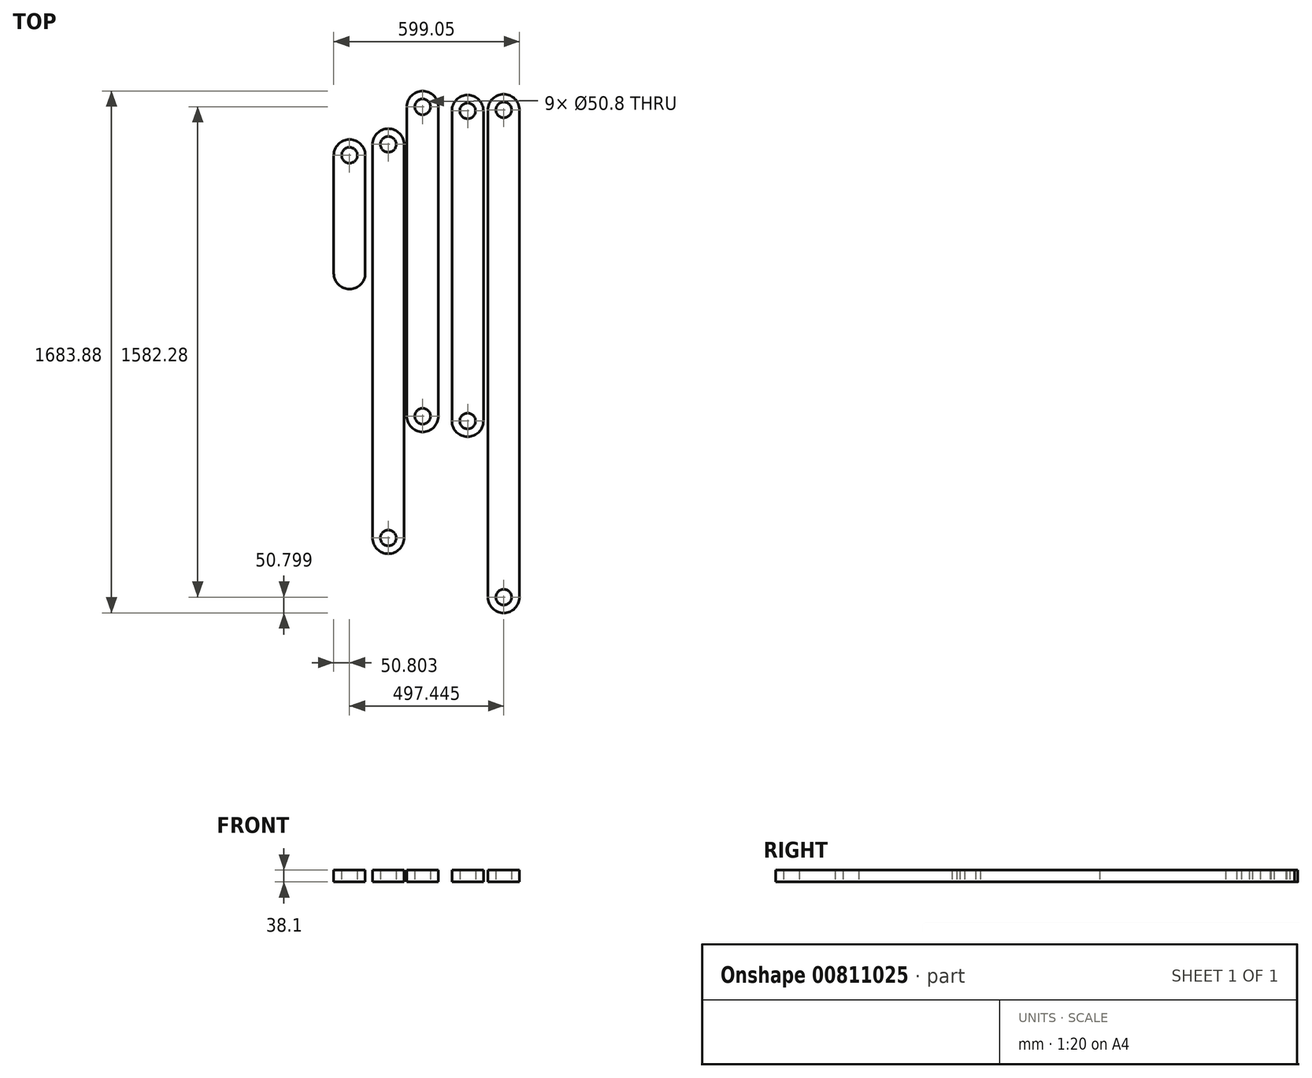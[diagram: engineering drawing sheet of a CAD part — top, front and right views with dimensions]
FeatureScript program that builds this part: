
annotation { "Feature Type Name" : "Feature", "Feature Type Description" : "" }
export const myFeature = defineFeature(function(context is Context, id is Id, definition is map)
    precondition{}
    {
        {
            var Q0;
            Q0=qCreatedBy(makeId("Top.planeOp"),FACE);
            var sketch = newSketch(context, id + "F0", { "sketchPlane" : qUnion([Q0])});
            skLineSegment(sketch, "E0", {"start": v(237.66, -949.52) * mm, "end": v(237.66, 51.24) * mm});
            skLineSegment(sketch, "E1", {"start": v(339.26, -949.52) * mm, "end": v(339.26, 51.24) * mm});
            skArc(sketch, "E2", {"start": v(237.66, -949.52) * mm, "mid": v(288.46, -1000.32) * mm, "end": v(339.26, -949.52) * mm});
            skArc(sketch, "E3", {"start": v(339.26, 51.24) * mm, "mid": v(288.46, 102.04) * mm, "end": v(237.66, 51.24) * mm});
            skLineSegment(sketch, "E4", {"start": v(237.66, 51.24) * mm, "end": v(339.26, 51.24) * mm, "construction": true});
            skLineSegment(sketch, "E5", {"start": v(237.66, -949.52) * mm, "end": v(339.26, -949.52) * mm, "construction": true});
            skLineSegment(sketch, "E6", {"start": v(-143.46, -473.04) * mm, "end": v(-143.46, -92.04) * mm});
            skLineSegment(sketch, "E7", {"start": v(-41.86, -473.04) * mm, "end": v(-41.86, -92.04) * mm});
            skArc(sketch, "E8", {"start": v(-143.46, -473.04) * mm, "mid": v(-92.66, -523.84) * mm, "end": v(-41.86, -473.04) * mm});
            skArc(sketch, "E9", {"start": v(-41.86, -92.04) * mm, "mid": v(-92.66, -41.24) * mm, "end": v(-143.46, -92.04) * mm});
            skLineSegment(sketch, "E10", {"start": v(-143.46, -92.04) * mm, "end": v(-41.86, -92.04) * mm, "construction": true});
            skLineSegment(sketch, "E11", {"start": v(-143.46, -473.04) * mm, "end": v(-41.86, -473.04) * mm, "construction": true});
            skLineSegment(sketch, "E12", {"start": v(92.52, -933.87) * mm, "end": v(92.52, 64.35) * mm});
            skLineSegment(sketch, "E13", {"start": v(194.12, -933.87) * mm, "end": v(194.12, 64.35) * mm});
            skArc(sketch, "E14", {"start": v(92.52, -933.87) * mm, "mid": v(143.32, -984.67) * mm, "end": v(194.12, -933.87) * mm});
            skArc(sketch, "E15", {"start": v(194.12, 64.35) * mm, "mid": v(143.32, 115.15) * mm, "end": v(92.52, 64.35) * mm});
            skLineSegment(sketch, "E16", {"start": v(92.52, 64.35) * mm, "end": v(194.12, 64.35) * mm, "construction": true});
            skLineSegment(sketch, "E17", {"start": v(92.52, -933.87) * mm, "end": v(194.12, -933.87) * mm, "construction": true});
            skLineSegment(sketch, "E18", {"start": v(-18.26, -1326.87) * mm, "end": v(-18.26, -56.87) * mm});
            skLineSegment(sketch, "E19", {"start": v(83.34, -1326.87) * mm, "end": v(83.34, -56.87) * mm});
            skArc(sketch, "E20", {"start": v(-18.26, -1326.87) * mm, "mid": v(32.54, -1377.67) * mm, "end": v(83.34, -1326.87) * mm});
            skArc(sketch, "E21", {"start": v(83.34, -56.87) * mm, "mid": v(32.54, -6.07) * mm, "end": v(-18.26, -56.87) * mm});
            skLineSegment(sketch, "E22", {"start": v(-18.26, -56.87) * mm, "end": v(83.34, -56.87) * mm, "construction": true});
            skLineSegment(sketch, "E23", {"start": v(-18.26, -1326.87) * mm, "end": v(83.34, -1326.87) * mm, "construction": true});
            skLineSegment(sketch, "E24", {"start": v(353.99, -1517.93) * mm, "end": v(353.99, 54.33) * mm});
            skLineSegment(sketch, "E25", {"start": v(455.59, -1517.93) * mm, "end": v(455.59, 54.33) * mm});
            skArc(sketch, "E26", {"start": v(353.99, -1517.93) * mm, "mid": v(404.79, -1568.73) * mm, "end": v(455.59, -1517.93) * mm});
            skArc(sketch, "E27", {"start": v(455.59, 54.33) * mm, "mid": v(404.79, 105.13) * mm, "end": v(353.99, 54.33) * mm});
            skLineSegment(sketch, "E28", {"start": v(353.99, 54.33) * mm, "end": v(455.59, 54.33) * mm, "construction": true});
            skLineSegment(sketch, "E29", {"start": v(353.99, -1517.93) * mm, "end": v(455.59, -1517.93) * mm, "construction": true});
            skCircle(sketch, "E30", {"center": v(288.46, -949.52) * mm, "radius": 25.4 * mm});
            skCircle(sketch, "E31", {"center": v(-92.66, -473.04) * mm, "radius": 25.4 * mm});
            skCircle(sketch, "E32", {"center": v(-92.66, -92.04) * mm, "radius": 25.4 * mm});
            skCircle(sketch, "E33", {"center": v(288.46, 51.24) * mm, "radius": 25.4 * mm});
            skCircle(sketch, "E34", {"center": v(143.32, -933.87) * mm, "radius": 25.4 * mm});
            skCircle(sketch, "E35", {"center": v(32.54, -1326.87) * mm, "radius": 25.4 * mm});
            skCircle(sketch, "E36", {"center": v(404.79, -1517.93) * mm, "radius": 25.4 * mm});
            skCircle(sketch, "E37", {"center": v(404.79, 54.33) * mm, "radius": 25.4 * mm});
            skCircle(sketch, "E38", {"center": v(143.32, 64.35) * mm, "radius": 25.4 * mm});
            skCircle(sketch, "E39", {"center": v(32.54, -56.87) * mm, "radius": 25.4 * mm});
            skSolve(sketch);
        }
        {
            var Q0;
            Q0=makeQuery(id+"F0.imprint","IMPRINT",FACE,{"disambiguationData":[TD([[makeQuery(id+"F0.imprint","IMPRINT",EDGE,{"derivedFrom":sQuery(id+"F0.wireOp",EDGE,"E6")}),-1.0]])]});
            var Q1;
            Q1=makeQuery(id+"F0.imprint","IMPRINT",FACE,{"disambiguationData":[TD([[makeQuery(id+"F0.imprint","IMPRINT",EDGE,{"derivedFrom":sQuery(id+"F0.wireOp",EDGE,"E18")}),-1.0]])]});
            var Q2;
            Q2=makeQuery(id+"F0.imprint","IMPRINT",FACE,{"disambiguationData":[TD([[makeQuery(id+"F0.imprint","IMPRINT",EDGE,{"derivedFrom":sQuery(id+"F0.wireOp",EDGE,"E12")}),-1.0]])]});
            var Q3;
            Q3=makeQuery(id+"F0.imprint","IMPRINT",FACE,{"disambiguationData":[TD([[makeQuery(id+"F0.imprint","IMPRINT",EDGE,{"derivedFrom":sQuery(id+"F0.wireOp",EDGE,"E0")}),-1.0]])]});
            var Q4;
            Q4=makeQuery(id+"F0.imprint","IMPRINT",FACE,{"disambiguationData":[TD([[makeQuery(id+"F0.imprint","IMPRINT",EDGE,{"derivedFrom":sQuery(id+"F0.wireOp",EDGE,"E24")}),-1.0]])]});
            var Q5;
            Q5=makeQuery(id+"F0.imprint","IMPRINT",FACE,{"disambiguationData":[TD([[makeQuery(id+"F0.imprint","IMPRINT",EDGE,{"derivedFrom":sQuery(id+"F0.wireOp",EDGE,"E31")}),1.0]])]});
            extrude(context, id + "F1", {"entities" : qUnion([Q0, Q1, Q2, Q3, Q4, Q5]), "depth" : 38.1 * mm, "offsetDistance" : 25.4 * mm});
        }
    });
